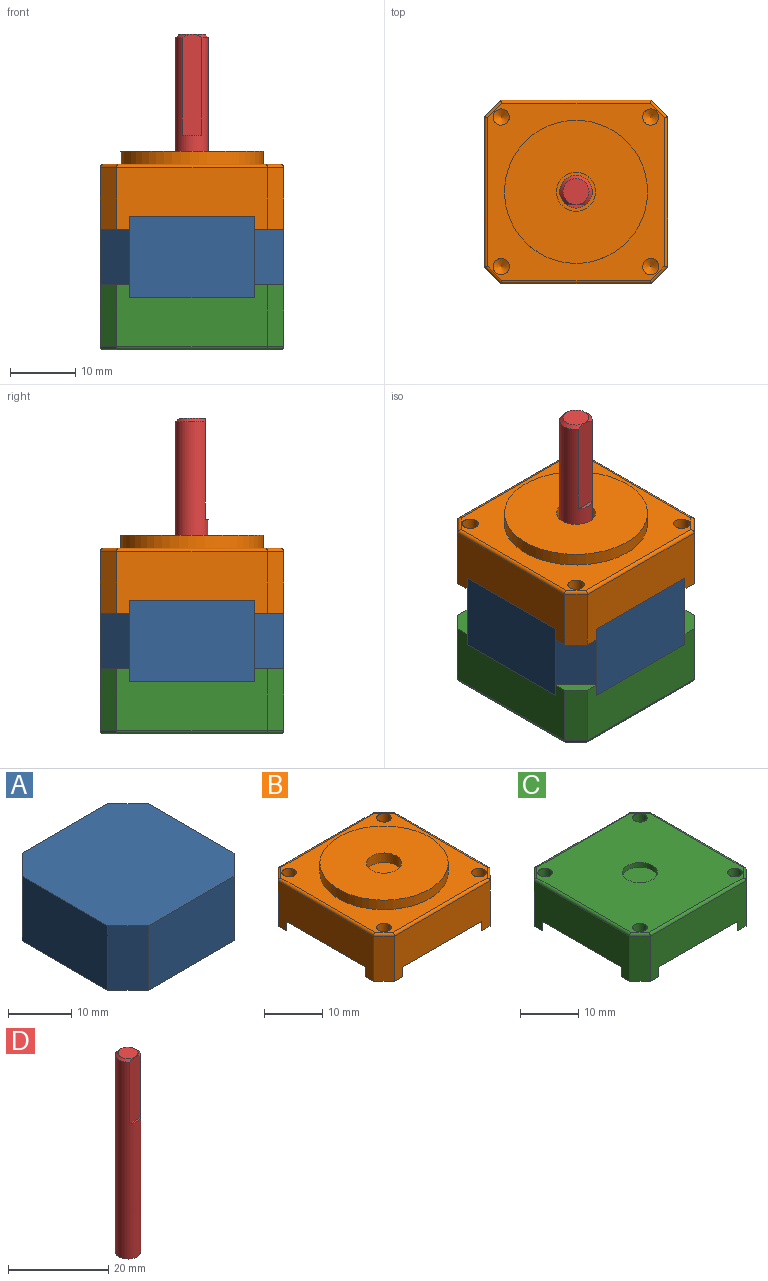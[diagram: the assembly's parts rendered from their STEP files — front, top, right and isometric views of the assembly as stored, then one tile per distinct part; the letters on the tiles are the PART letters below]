
ASSEMBLY  parts=4 mates=3
PART A: 10 faces, bbox 28.2x28.2x12.5 mm
  f0: plane 19.2x12.5mm, normal (0,1,0), area 240mm2, adj f1,f7,f8,f9
  f1: plane 12.5x4.5mm, normal (-0.71,0.71,0), area 79.5mm2, adj f0,f2,f8,f9
  f2: plane 19.2x12.5mm, normal (-1,0,0), area 240mm2, adj f1,f3,f8,f9
  f3: plane 12.5x4.5mm, normal (-0.71,-0.71,0), area 79.5mm2, adj f2,f4,f8,f9
  f4: plane 19.2x12.5mm, normal (0,-1,0), area 240mm2, adj f3,f5,f8,f9
  f5: plane 12.5x4.5mm, normal (0.71,-0.71,0), area 79.5mm2, adj f4,f6,f8,f9
  f6: plane 19.2x12.5mm, normal (1,0,0), area 240mm2, adj f5,f7,f8,f9
  f7: plane 12.5x4.5mm, normal (0.71,0.71,0), area 79.5mm2, adj f0,f6,f8,f9
  f8: plane 28.2x28.2mm, normal (0,0,1), area 754.7mm2, adj f0,f1,f2,f3,f4,f5,f6,f7
  f9: plane 28.2x28.2mm, normal (0,0,-1), area 754.7mm2, adj f0,f1,f2,f3,f4,f5,f6,f7
PART B: 38 faces, bbox 28.2x28.2x12 mm
  f0: plane 28.2x28.2mm, normal (0,0,-1), area 754.7mm2, adj f1,f3,f5,f7,f14,f16,f18,f20
  f1: plane 23.2x9.5mm, normal (0,-1,0), area 182mm2, adj f0,f2,f8,f16,f17,f20,f21,f37
  f2: plane 9.5x2.5mm, normal (0.71,-0.71,0), area 33.6mm2, adj f1,f3,f17,f35
  f3: plane 23.2x9.5mm, normal (1,0,0), area 182mm2, adj f0,f2,f4,f14,f15,f16,f17,f33
  f4: plane 9.5x2.5mm, normal (0.71,0.71,0), area 33.6mm2, adj f3,f5,f15,f31
  f5: plane 23.2x9.5mm, normal (0,1,0), area 182mm2, adj f0,f4,f6,f14,f15,f18,f19,f30
  f6: plane 9.5x2.5mm, normal (-0.71,0.71,0), area 33.6mm2, adj f5,f7,f19,f32
  f7: plane 23.2x9.5mm, normal (-1,0,0), area 182mm2, adj f0,f6,f8,f18,f19,f20,f21,f34
  f8: plane 9.5x2.5mm, normal (-0.71,-0.71,0), area 33.6mm2, adj f1,f7,f21,f36
  f9: plane 27.2x27.2mm, normal (0,0,1), area 330.3mm2, adj f11,f23,f25,f27,f29,f30,f31,f32
  f10: cylinder r=3mm len=6mm, axis (0,0,-1), area 37.7mm2, adj f12,f13
  f11: cylinder r=11mm len=22mm, axis (0,0,-1), area 138.2mm2, adj f9,f12
  f12: plane 22x22mm, normal (0,0,1), area 351.9mm2, adj f10,f11
  f13: plane 6x6mm, normal (0,0,1), area 28.3mm2, adj f10
  f14: plane 4.5x4.5mm, normal (-0.71,-0.71,0), area 12.7mm2, adj f0,f3,f5,f15
  f15: plane 4.5x4.5mm, normal (0,0,-1), area 7mm2, adj f3,f4,f5,f14
  f16: plane 4.5x4.5mm, normal (-0.71,0.71,0), area 12.7mm2, adj f0,f1,f3,f17
  f17: plane 4.5x4.5mm, normal (0,0,-1), area 7mm2, adj f1,f2,f3,f16
  f18: plane 4.5x4.5mm, normal (0.71,-0.71,0), area 12.7mm2, adj f0,f5,f7,f19
  f19: plane 4.5x4.5mm, normal (0,0,-1), area 7mm2, adj f5,f6,f7,f18
  f20: plane 4.5x4.5mm, normal (0.71,0.71,0), area 12.7mm2, adj f0,f1,f7,f21
  f21: plane 4.5x4.5mm, normal (0,0,-1), area 7mm2, adj f1,f7,f8,f20
  f22: cone r=0mm half-angle=59deg, axis (0,0,1), area 5.7mm2, adj f23
  f23: cylinder r=1.25mm len=3mm, axis (0,0,1), area 23.6mm2, adj f9,f22
  f24: cone r=0mm half-angle=59deg, axis (0,0,1), area 5.7mm2, adj f25
  f25: cylinder r=1.25mm len=3mm, axis (0,0,1), area 23.6mm2, adj f9,f24
  f26: cone r=0mm half-angle=59deg, axis (0,0,1), area 5.7mm2, adj f27
  f27: cylinder r=1.25mm len=3mm, axis (0,0,1), area 23.6mm2, adj f9,f26
  f28: cone r=0mm half-angle=59deg, axis (0,0,1), area 5.7mm2, adj f29
  f29: cylinder r=1.25mm len=3mm, axis (0,0,1), area 23.6mm2, adj f9,f28
  f30: cylinder r=0.5mm len=23.2mm, axis (-1,0,0), area 18.1mm2, adj f5,f9,f31,f32
  f31: cylinder r=0.5mm len=2.85mm, axis (-0.71,0.71,0), area 2.7mm2, adj f4,f9,f30,f33
  f32: cylinder r=0.5mm len=2.85mm, axis (-0.71,-0.71,0), area 2.7mm2, adj f6,f9,f30,f34
  f33: cylinder r=0.5mm len=23.2mm, axis (0,1,0), area 18.1mm2, adj f3,f9,f31,f35
  f34: cylinder r=0.5mm len=23.2mm, axis (0,-1,0), area 18.1mm2, adj f7,f9,f32,f36
  f35: cylinder r=0.5mm len=2.85mm, axis (0.71,0.71,0), area 2.7mm2, adj f2,f9,f33,f37
  f36: cylinder r=0.5mm len=2.85mm, axis (0.71,-0.71,0), area 2.7mm2, adj f8,f9,f34,f37
  f37: cylinder r=0.5mm len=23.2mm, axis (1,0,0), area 18.1mm2, adj f1,f9,f35,f36
PART C: 36 faces, bbox 28.2x28.2x10 mm
  f0: plane 28.2x28.2mm, normal (0,0,-1), area 754.7mm2, adj f1,f3,f5,f7,f12,f14,f16,f18
  f1: plane 23.2x9.5mm, normal (0,1,0), area 182mm2, adj f0,f2,f8,f14,f15,f18,f19,f30
  f2: plane 9.5x2.5mm, normal (-0.71,0.71,0), area 33.6mm2, adj f1,f3,f19,f32
  f3: plane 23.2x9.5mm, normal (-1,0,0), area 182mm2, adj f0,f2,f4,f16,f17,f18,f19,f34
  f4: plane 9.5x2.5mm, normal (-0.71,-0.71,0), area 33.6mm2, adj f3,f5,f17,f35
  f5: plane 23.2x9.5mm, normal (0,-1,0), area 182mm2, adj f0,f4,f6,f12,f13,f16,f17,f33
  f6: plane 9.5x2.5mm, normal (0.71,-0.71,0), area 33.6mm2, adj f5,f7,f13,f31
  f7: plane 23.2x9.5mm, normal (1,0,0), area 182mm2, adj f0,f6,f8,f12,f13,f14,f15,f29
  f8: plane 9.5x2.5mm, normal (0.71,0.71,0), area 33.6mm2, adj f1,f7,f15,f28
  f9: plane 27.2x27.2mm, normal (0,0,1), area 682.2mm2, adj f10,f21,f23,f25,f27,f28,f29,f30
  f10: cylinder r=3mm len=6mm, axis (0,0,1), area 18.8mm2, adj f9,f11
  f11: plane 6x6mm, normal (0,0,1), area 28.3mm2, adj f10
  f12: plane 4.5x4.5mm, normal (-0.71,0.71,0), area 12.7mm2, adj f0,f5,f7,f13
  f13: plane 4.5x4.5mm, normal (0,0,-1), area 7mm2, adj f5,f6,f7,f12
  f14: plane 4.5x4.5mm, normal (-0.71,-0.71,0), area 12.7mm2, adj f0,f1,f7,f15
  f15: plane 4.5x4.5mm, normal (0,0,-1), area 7mm2, adj f1,f7,f8,f14
  f16: plane 4.5x4.5mm, normal (0.71,0.71,0), area 12.7mm2, adj f0,f3,f5,f17
  f17: plane 4.5x4.5mm, normal (0,0,-1), area 7mm2, adj f3,f4,f5,f16
  f18: plane 4.5x4.5mm, normal (0.71,-0.71,0), area 12.7mm2, adj f0,f1,f3,f19
  f19: plane 4.5x4.5mm, normal (0,0,-1), area 7mm2, adj f1,f2,f3,f18
  f20: cone r=0mm half-angle=59deg, axis (0,0,1), area 5.7mm2, adj f21
  f21: cylinder r=1.25mm len=3mm, axis (0,0,1), area 23.6mm2, adj f9,f20
  f22: cone r=0mm half-angle=59deg, axis (0,0,1), area 5.7mm2, adj f23
  f23: cylinder r=1.25mm len=3mm, axis (0,0,1), area 23.6mm2, adj f9,f22
  f24: cone r=0mm half-angle=59deg, axis (0,0,1), area 5.7mm2, adj f25
  f25: cylinder r=1.25mm len=3mm, axis (0,0,1), area 23.6mm2, adj f9,f24
  f26: cone r=0mm half-angle=59deg, axis (0,0,1), area 5.7mm2, adj f27
  f27: cylinder r=1.25mm len=3mm, axis (0,0,1), area 23.6mm2, adj f9,f26
  f28: cylinder r=0.5mm len=2.85mm, axis (-0.71,0.71,0), area 2.7mm2, adj f8,f9,f29,f30
  f29: cylinder r=0.5mm len=23.2mm, axis (0,1,0), area 18.1mm2, adj f7,f9,f28,f31
  f30: cylinder r=0.5mm len=23.2mm, axis (-1,0,0), area 18.1mm2, adj f1,f9,f28,f32
  f31: cylinder r=0.5mm len=2.85mm, axis (0.71,0.71,0), area 2.7mm2, adj f6,f9,f29,f33
  f32: cylinder r=0.5mm len=2.85mm, axis (-0.71,-0.71,0), area 2.7mm2, adj f2,f9,f30,f34
  f33: cylinder r=0.5mm len=23.2mm, axis (1,0,0), area 18.1mm2, adj f5,f9,f31,f35
  f34: cylinder r=0.5mm len=23.2mm, axis (0,-1,0), area 18.1mm2, adj f3,f9,f32,f35
  f35: cylinder r=0.5mm len=2.85mm, axis (0.71,-0.71,0), area 2.7mm2, adj f4,f9,f33,f34
PART D: 6 faces, bbox 5x5x48.5 mm
  f0: cylinder r=2.5mm len=48mm, axis (0,0,-1), area 705.7mm2, adj f2,f3,f4,f5
  f1: plane 4x4mm, normal (0,0,1), area 12.6mm2, adj f4
  f2: plane 15.5x3mm, normal (0,-1,0), area 46mm2, adj f0,f3,f4
  f3: plane 3x0.5mm, normal (0,0,1), area 1mm2, adj f0,f2
  f4: cone r=2mm half-angle=45deg, axis (0,0,-1), area 8.6mm2, adj f0,f1,f2
  f5: plane 5x5mm, normal (0,0,-1), area 19.6mm2, adj f0
PLACE A rot(axis=(1,0,0),180deg) t=(-46.32,-16.02,6.23)mm
PLACE B t=(-6.32,-16.02,14.23)mm
PLACE C rot(axis=(1,0,0),180deg) t=(43.68,-16.02,-14.27)mm
PLACE D t=(-6.32,23.98,14.23)mm
MATE fastened A.f9 <-> B.f10  axis (0,0,1) through (-6.32,-16.02,6.23)mm
MATE fastened C.f10 <-> A.f8  axis (0,0,1) through (-6.32,-16.02,-6.27)mm
MATE revolute D.f0 <-> B.f10  axis (0,0,-1) through (-6.32,-16.02,14.23)mm
